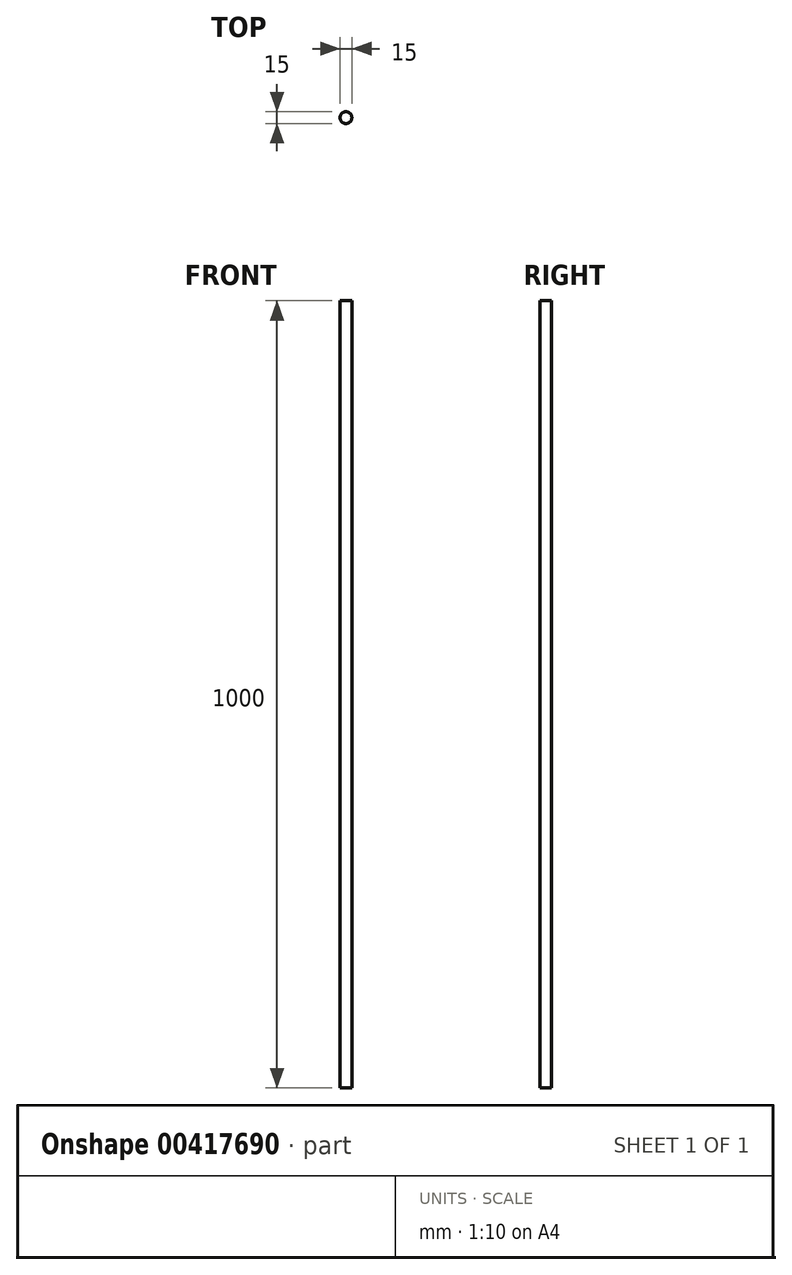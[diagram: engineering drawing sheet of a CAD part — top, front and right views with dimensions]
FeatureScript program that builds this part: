
annotation { "Feature Type Name" : "Feature", "Feature Type Description" : "" }
export const myFeature = defineFeature(function(context is Context, id is Id, definition is map)
    precondition{}
    {
        {
            var Q0;
            Q0=qCreatedBy(makeId("Top.planeOp"),FACE);
            var sketch = newSketch(context, id + "F0", { "sketchPlane" : qUnion([Q0])});
            skCircle(sketch, "E0", {"center": v(0, 0) * mm, "radius": 7.5 * mm});
            skSolve(sketch);
        }
        {
            var Q0;
            Q0=sQuery(id+"F0.wireOp",EDGE,"E0");
            extrude(context, id + "F1", {"bodyType" : ToolBodyType.SURFACE, "surfaceEntities" : qUnion([Q0]), "depth" : 1000 * mm});
        }
        {
            var Q0;
            Q0=qCreatedBy(makeId("Top.planeOp"),FACE);
            var sketch = newSketch(context, id + "F2", { "sketchPlane" : qUnion([Q0])});
            skCircle(sketch, "E1", {"center": v(0, 70) * mm, "radius": 7.5 * mm});
            skSolve(sketch);
        }
        {
            var Q0;
            Q0=qCreatedBy(makeId("Right.planeOp"),FACE);
            var sketch = newSketch(context, id + "F3", { "sketchPlane" : qUnion([Q0])});
            skFitSpline(sketch, "E2", {"points": [v(70.91, 0) * mm, v(240.87, 21.7) * mm, v(397.85, 132.95) * mm, v(403.4, 256.33) * mm, v(328.89, 383.76) * mm, v(191, 860.6) * mm], "startDerivative": vector(36.58, 877.1) * mm, "endDerivative": vector(1864.65, 1790.43) * mm});
            skSolve(sketch);
        }
        {
            var Q0;
            Q0=qCreatedBy(makeId("Top.planeOp"),FACE);
            var sketch = newSketch(context, id + "F4", { "sketchPlane" : qUnion([Q0])});
            skCircle(sketch, "E3", {"center": v(45.73, 26.24) * mm, "radius": 7.5 * mm});
            skSolve(sketch);
        }
        {
            var Q0;
            Q0=qCreatedBy(makeId("Top.planeOp"),FACE);
            var sketch = newSketch(context, id + "F5", { "sketchPlane" : qUnion([Q0])});
            skCircle(sketch, "E4", {"center": v(-75.04, 0) * mm, "radius": 7.5 * mm});
            skSolve(sketch);
        }
        {
            var Q0;
            Q0=qCreatedBy(makeId("Top.planeOp"),FACE);
            var sketch = newSketch(context, id + "F6", { "sketchPlane" : qUnion([Q0])});
            skCircle(sketch, "E5", {"center": v(-46.25, -78.7) * mm, "radius": 7.5 * mm});
            skSolve(sketch);
        }
        {
            var Q0;
            Q0=qCreatedBy(makeId("Front.planeOp"),FACE);
            var sketch = newSketch(context, id + "F7", { "sketchPlane" : qUnion([Q0])});
            skFitSpline(sketch, "E6", {"points": [v(-74.98, 0) * mm, v(-244.67, 27.67) * mm, v(-397.7, 239.78) * mm, v(-240.13, 524.62) * mm, v(-82.56, 729.16) * mm, v(-129.81, 815.52) * mm], "startDerivative": vector(23.5, 1219.51) * mm, "endDerivative": vector(-745.27, 820.4) * mm});
            skSolve(sketch);
        }
        {
            var Q0;
            Q0=qCreatedBy(makeId("Top.planeOp"),FACE);
            var sketch = newSketch(context, id + "F8", { "sketchPlane" : qUnion([Q0])});
            skLineSegment(sketch, "E7", {"start": v(0, 0) * mm, "end": v(-45.44, -77.7) * mm});
            skSolve(sketch);
        }
        {
            var Q0;
            Q0=qCreatedBy(makeId("Top.planeOp"),FACE);
            var sketch = newSketch(context, id + "F9", { "sketchPlane" : qUnion([Q0])});
            skLineSegment(sketch, "E8", {"start": v(0, 0) * mm, "end": v(45.75, 27.25) * mm});
            skSolve(sketch);
        }
        {
            var Q0;
            Q0=sQuery(id+"F8.wireOp",EDGE,"E7");
            extrude(context, id + "F10", {"bodyType" : ToolBodyType.SURFACE, "surfaceEntities" : qUnion([Q0]), "depth" : 351 * mm, "offsetDistance" : 25 * mm});
        }
        {
            var Q0;
            Q0=makeQuery(id+"F10.opExtrude","SWEPT_FACE",FACE,{"disambiguationData":[OSD([sQuery(id+"F8.wireOp",EDGE,"E7")])]});
            cPlane(context, id + "F11", {"entities" : qUnion([Q0]), "cplaneType" : CPlaneType.OFFSET, "offset" : 0 * mm, "width" : 150 * mm, "height" : 150 * mm});
        }
        {
            var Q0;
            Q0=sQuery(id+"F9.wireOp",EDGE,"E8");
            extrude(context, id + "F12", {"bodyType" : ToolBodyType.SURFACE, "surfaceEntities" : qUnion([Q0]), "depth" : 529 * mm, "offsetDistance" : 25 * mm});
        }
        {
            var Q0;
            Q0=makeQuery(id+"F12.opExtrude","SWEPT_FACE",FACE,{"disambiguationData":[OSD([sQuery(id+"F9.wireOp",EDGE,"E8")])]});
            cPlane(context, id + "F13", {"entities" : qUnion([Q0]), "cplaneType" : CPlaneType.OFFSET, "offset" : 0 * mm, "width" : 150 * mm, "height" : 150 * mm});
        }
        {
            var Q0;
            Q0=qCreatedBy(id+"F13.planeOp",FACE);
            var sketch = newSketch(context, id + "F14", { "sketchPlane" : qUnion([Q0])});
            skFitSpline(sketch, "E9", {"points": [v(52.26, 0) * mm, v(167.63, 17.28) * mm, v(286.66, 169.27) * mm, v(160.3, 522.7) * mm, v(92.55, 680.2) * mm, v(231.08, 894.3) * mm], "startDerivative": vector(200.02, 1329.25) * mm, "endDerivative": vector(709.24, 666.1) * mm});
            skSolve(sketch);
        }
        {
            var Q0;
            Q0=qCreatedBy(id+"F11.planeOp",FACE);
            var sketch = newSketch(context, id + "F15", { "sketchPlane" : qUnion([Q0])});
            skFitSpline(sketch, "E10", {"points": [v(95.07, 0) * mm, v(174.26, 14.12) * mm, v(293.26, 85.82) * mm, v(309.61, 298.52) * mm, v(150.62, 631.85) * mm, v(154.93, 767.35) * mm, v(175.06, 782.05) * mm], "startDerivative": vector(123.05, 1354.32) * mm, "endDerivative": vector(-1321.06, -1181.66) * mm});
            skSolve(sketch);
        }
        {
            var Q0;
            Q0=makeQuery(id+"F10.opExtrude","SWEPT_BODY",BODY,{"disambiguationData":[OSD([sQuery(id+"F8.wireOp",EDGE,"E7")])]});
            deleteBodies(context, id + "F16", {"entities" : qUnion([Q0])});
        }
        {
            var Q0;
            Q0=makeQuery(id+"F12.opExtrude","SWEPT_BODY",BODY,{"disambiguationData":[OSD([sQuery(id+"F9.wireOp",EDGE,"E8")])]});
            deleteBodies(context, id + "F17", {"entities" : qUnion([Q0])});
        }
    });
